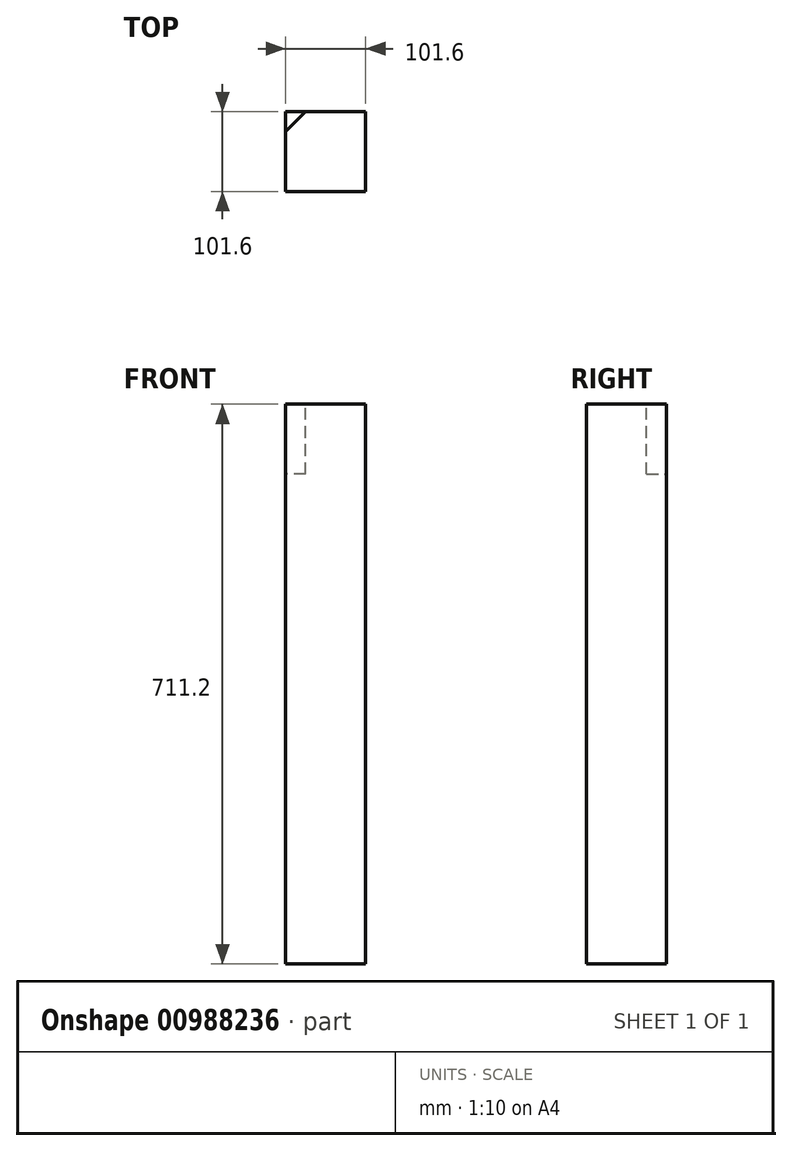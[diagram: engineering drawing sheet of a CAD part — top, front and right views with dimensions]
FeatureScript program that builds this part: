
annotation { "Feature Type Name" : "Feature", "Feature Type Description" : "" }
export const myFeature = defineFeature(function(context is Context, id is Id, definition is map)
    precondition{}
    {
        {
            var Q0;
            Q0=qCreatedBy(makeId("Right.planeOp"),FACE);
            var sketch = newSketch(context, id + "F0", { "sketchPlane" : qUnion([Q0])});
            skLineSegment(sketch, "E0.bottom", {"start": v(1.2, 0) * mm, "end": v(102.8, 0) * mm});
            skLineSegment(sketch, "E0.top", {"start": v(1.2, 711.2) * mm, "end": v(102.8, 711.2) * mm});
            skLineSegment(sketch, "E0.left", {"start": v(1.2, 0) * mm, "end": v(1.2, 711.2) * mm});
            skLineSegment(sketch, "E0.right", {"start": v(102.8, 0) * mm, "end": v(102.8, 711.2) * mm});
            skSolve(sketch);
        }
        {
            var Q0;
            Q0 = qSketchRegion(id + "F0", true);
            extrude(context, id + "F1", {"entities" : qUnion([Q0]), "depth" : 101.6 * mm, "offsetDistance" : 25.4 * mm});
        }
        {
            var Q0;
            Q0=makeQuery(id+"F1.opExtrude","SWEPT_FACE",FACE,{"disambiguationData":[OSD([sQuery(id+"F0.wireOp",EDGE,"E0.top")])]});
            var sketch = newSketch(context, id + "F2", { "sketchPlane" : qUnion([Q0])});
            skLineSegment(sketch, "E1", {"start": v(0, 102.8) * mm, "end": v(0, 77.4) * mm});
            skLineSegment(sketch, "E2", {"start": v(0, 77.4) * mm, "end": v(25.4, 102.8) * mm});
            skLineSegment(sketch, "E3", {"start": v(25.4, 102.8) * mm, "end": v(0, 102.8) * mm});
            skSolve(sketch);
        }
        {
            var Q0;
            Q0 = qSketchRegion(id + "F2", true);
            extrude(context, id + "F3", {"entities" : qUnion([Q0]), "operationType" : NewBodyOperationType.REMOVE, "oppositeDirection" : true, "depth" : 88.9 * mm, "offsetDistance" : 25.4 * mm});
        }
    });
